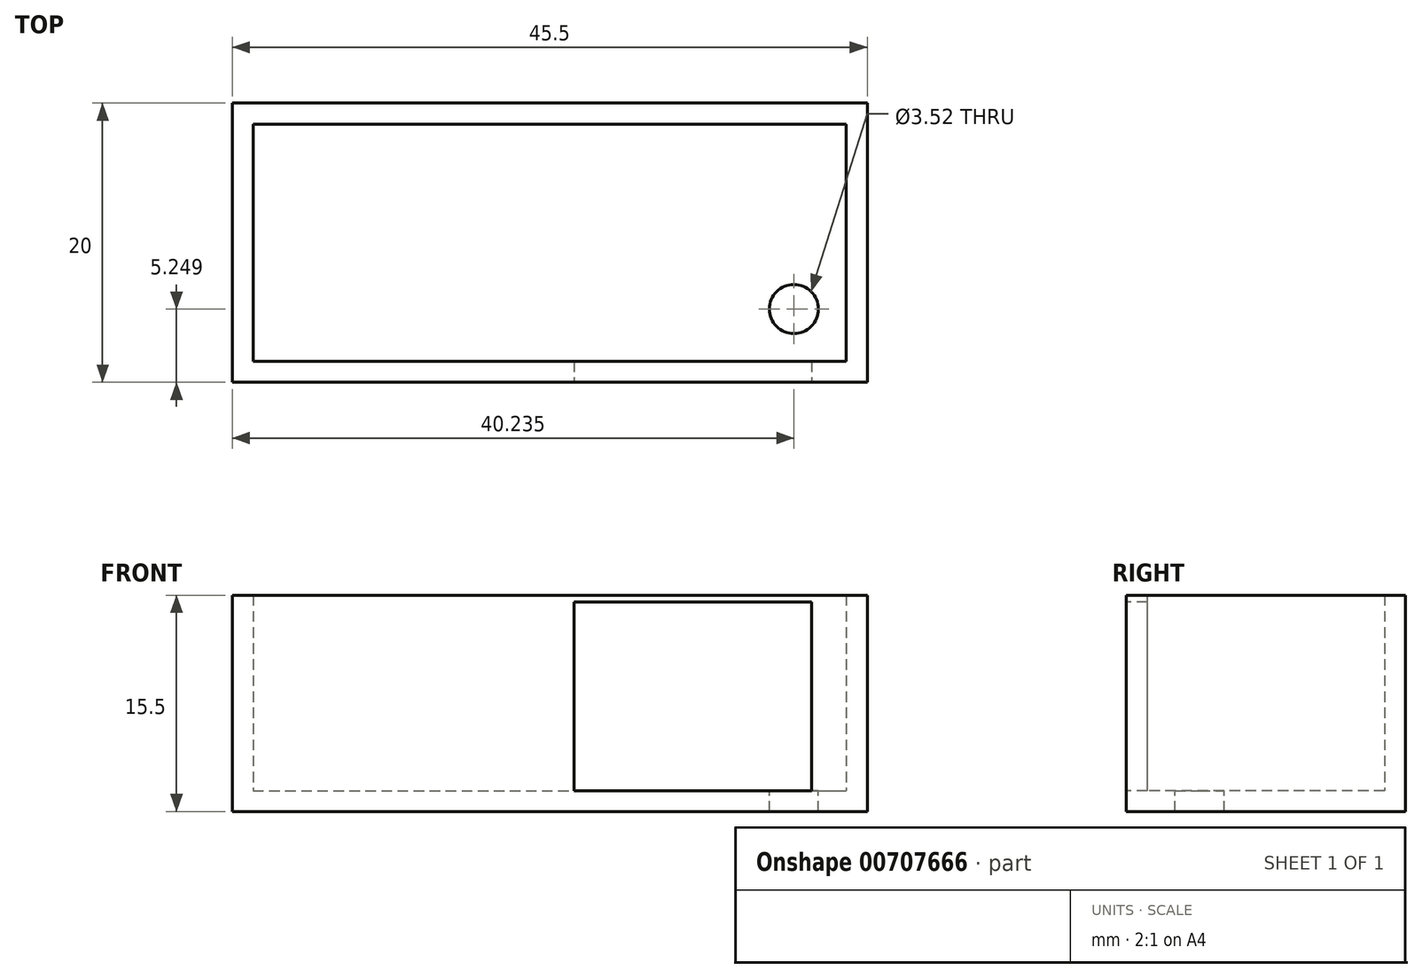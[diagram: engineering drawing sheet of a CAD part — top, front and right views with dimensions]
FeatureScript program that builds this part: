
annotation { "Feature Type Name" : "Feature", "Feature Type Description" : "" }
export const myFeature = defineFeature(function(context is Context, id is Id, definition is map)
    precondition{}
    {
        {
            var Q0;
            Q0=qCreatedBy(makeId("Top.planeOp"),FACE);
            var sketch = newSketch(context, id + "F0", { "sketchPlane" : qUnion([Q0])});
            skLineSegment(sketch, "E0.bottom", {"start": v(-19.77, 8.68) * mm, "end": v(22.73, 8.68) * mm});
            skLineSegment(sketch, "E0.top", {"start": v(-19.77, -8.32) * mm, "end": v(22.73, -8.32) * mm});
            skLineSegment(sketch, "E0.left", {"start": v(-19.77, 8.68) * mm, "end": v(-19.77, -8.32) * mm});
            skLineSegment(sketch, "E0.right", {"start": v(22.73, 8.68) * mm, "end": v(22.73, -8.32) * mm});
            skLineSegment(sketch, "E1.0", {"start": v(-21.27, 10.18) * mm, "end": v(24.23, 10.18) * mm});
            skLineSegment(sketch, "E1.1", {"start": v(-21.27, 10.18) * mm, "end": v(-21.27, -9.82) * mm});
            skLineSegment(sketch, "E1.2", {"start": v(-21.27, -9.82) * mm, "end": v(24.23, -9.82) * mm});
            skLineSegment(sketch, "E1.3", {"start": v(24.23, 10.18) * mm, "end": v(24.23, -9.82) * mm});
            skCircle(sketch, "E2", {"center": v(18.96, -4.57) * mm, "radius": 1.76 * mm});
            skSolve(sketch);
        }
        {
            var Q0;
            Q0=makeQuery(id+"F0.imprint","IMPRINT",FACE,{"disambiguationData":[TD([[makeQuery(id+"F0.imprint","IMPRINT",EDGE,{"derivedFrom":sQuery(id+"F0.wireOp",EDGE,"E0.bottom")}),-1.0]])]});
            var Q1;
            Q1=makeQuery(id+"F0.imprint","IMPRINT",FACE,{"disambiguationData":[TD([[makeQuery(id+"F0.imprint","IMPRINT",EDGE,{"derivedFrom":sQuery(id+"F0.wireOp",EDGE,"E0.bottom")}),1.0]])]});
            extrude(context, id + "F1", {"entities" : qUnion([Q0, Q1]), "oppositeDirection" : true, "depth" : 1.5 * mm, "offsetDistance" : 25 * mm});
        }
        {
            var Q0;
            Q0 = qSketchRegion(id + "F0", true);
            extrude(context, id + "F2", {"entities" : qUnion([Q0]), "operationType" : NewBodyOperationType.ADD, "depth" : 14 * mm, "offsetDistance" : 25 * mm});
        }
        {
            var Q0;
            {var subQ0=sQuery(id+"F0.wireOp",EDGE,"E1.2");Q0=makeQuery(id+"F2.boolean.opBoolean","MERGE",FACE,{"derivedFrom":[makeQuery(id+"F1.opExtrude","SWEPT_FACE",FACE,{"disambiguationData":[OSD([subQ0])]}),makeQuery(id+"F2.opExtrude","SWEPT_FACE",FACE,{"disambiguationData":[OSD([subQ0])]})]});}
            var sketch = newSketch(context, id + "F3", { "sketchPlane" : qUnion([Q0])});
            skLineSegment(sketch, "E3.bottom", {"start": v(3.23, 0) * mm, "end": v(20.23, 0) * mm});
            skLineSegment(sketch, "E3.top", {"start": v(3.23, 13.5) * mm, "end": v(20.23, 13.5) * mm});
            skLineSegment(sketch, "E3.left", {"start": v(3.23, 0) * mm, "end": v(3.23, 13.5) * mm});
            skLineSegment(sketch, "E3.right", {"start": v(20.23, 0) * mm, "end": v(20.23, 13.5) * mm});
            skSolve(sketch);
        }
        {
            var Q0;
            Q0=makeQuery(id+"F3.imprint","IMPRINT",FACE,{"disambiguationData":[TD([[makeQuery(id+"F3.imprint","IMPRINT",EDGE,{"derivedFrom":sQuery(id+"F3.wireOp",EDGE,"E3.bottom")}),1.0]])]});
            extrude(context, id + "F4", {"entities" : qUnion([Q0]), "operationType" : NewBodyOperationType.REMOVE, "oppositeDirection" : true, "depth" : 2 * mm, "offsetDistance" : 25 * mm});
        }
    });
